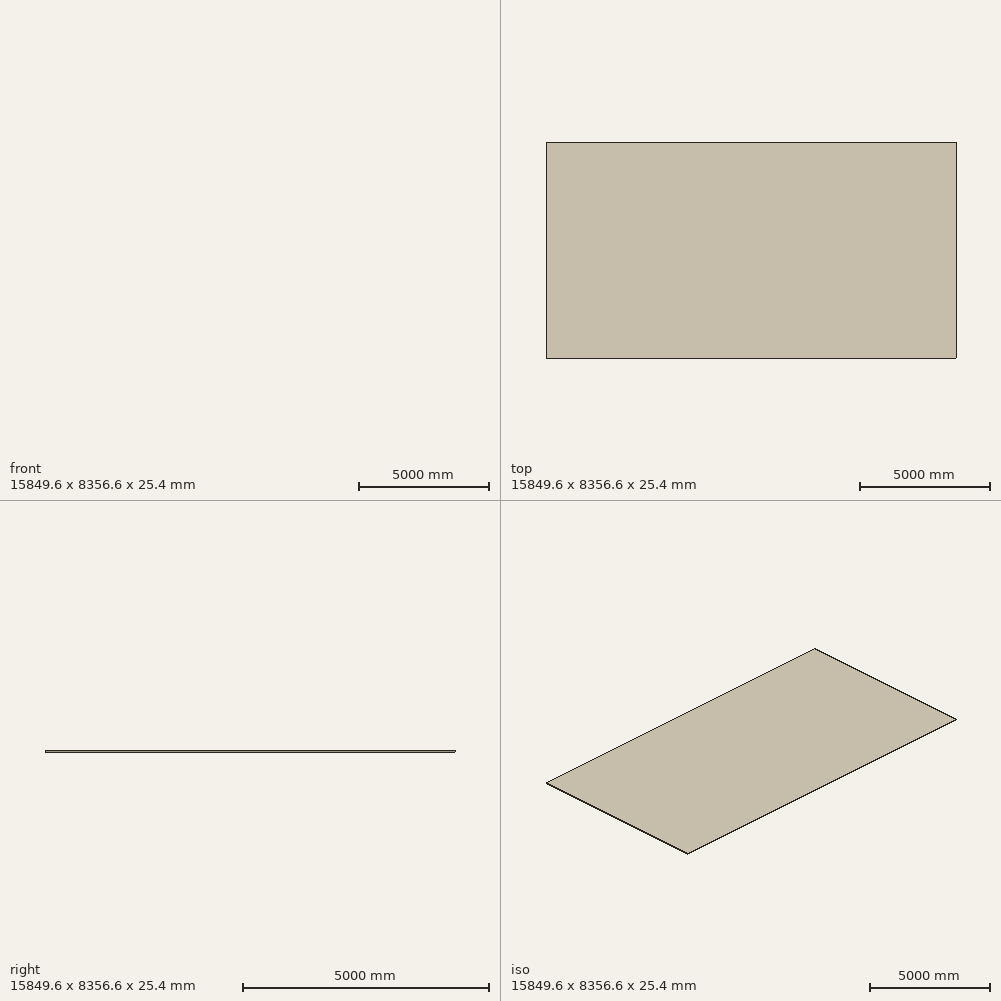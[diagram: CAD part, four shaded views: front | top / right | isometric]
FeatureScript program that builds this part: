
annotation { "Feature Type Name" : "Feature", "Feature Type Description" : "" }
export const myFeature = defineFeature(function(context is Context, id is Id, definition is map)
    precondition{}
    {
        {
            var Q0;
            Q0=qCreatedBy(makeId("Top.planeOp"),FACE);
            var sketch = newSketch(context, id + "F0", { "sketchPlane" : qUnion([Q0])});
            skLineSegment(sketch, "E0.bottom", {"start": v(-7927.26, 2555.09) * mm, "end": v(7922.34, 2555.09) * mm});
            skLineSegment(sketch, "E0.top", {"start": v(-7927.26, -5801.51) * mm, "end": v(7922.34, -5801.51) * mm});
            skLineSegment(sketch, "E0.left", {"start": v(-7927.26, 2555.09) * mm, "end": v(-7927.26, -5801.51) * mm});
            skLineSegment(sketch, "E0.right", {"start": v(7922.34, 2555.09) * mm, "end": v(7922.34, -5801.51) * mm});
            skSolve(sketch);
        }
        {
            var Q0;
            Q0 = qSketchRegion(id + "F0", true);
            extrude(context, id + "F1", {"entities" : qUnion([Q0]), "depth" : 25.4 * mm, "offsetDistance" : 25.4 * mm});
        }
    });
